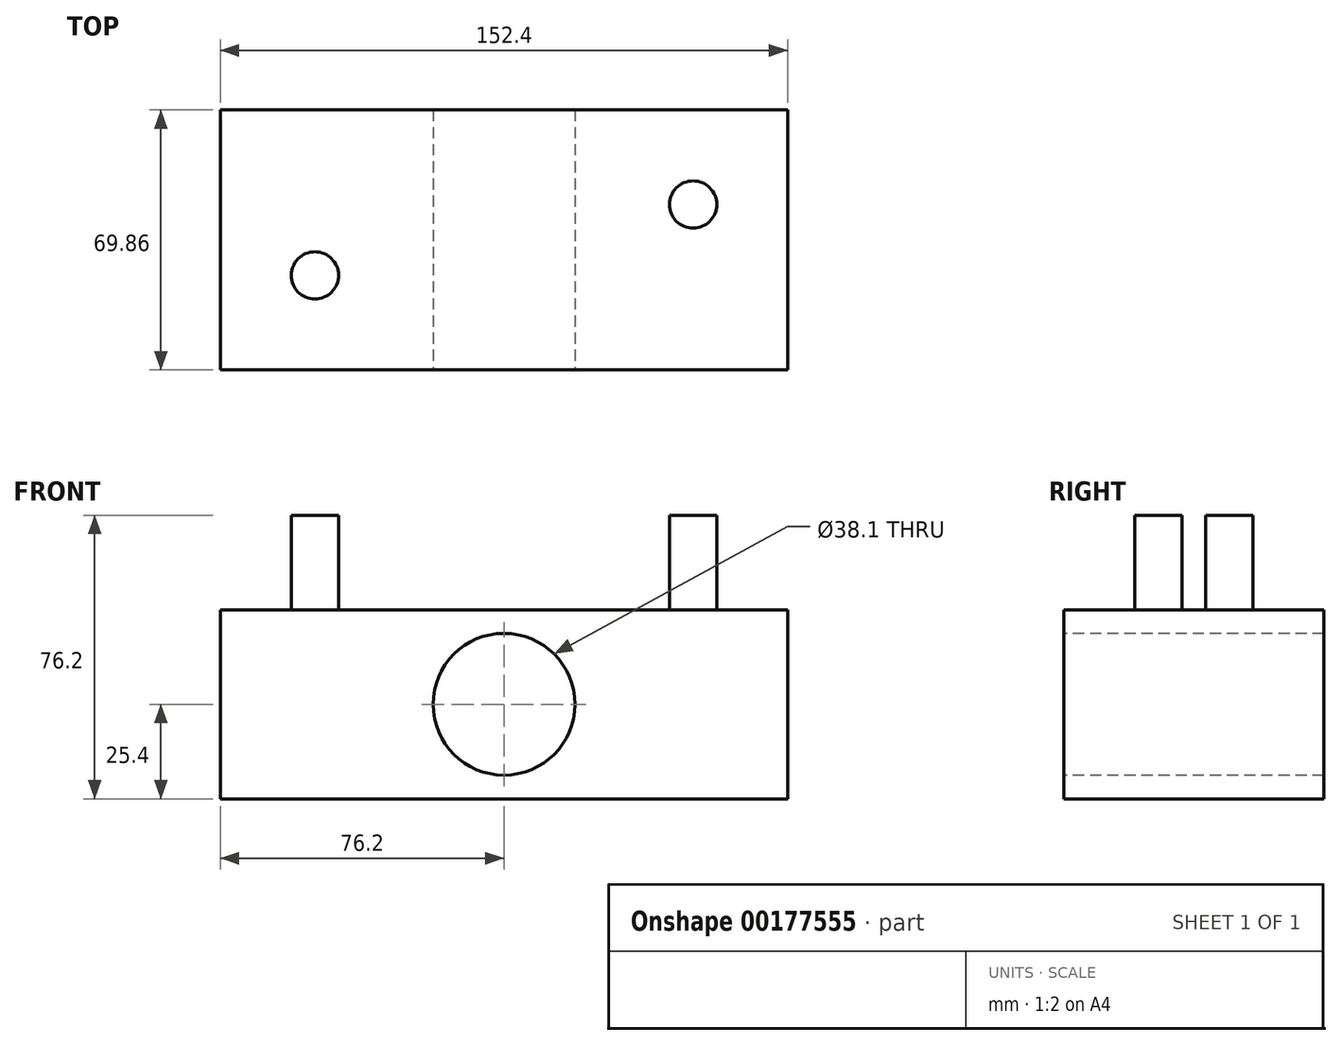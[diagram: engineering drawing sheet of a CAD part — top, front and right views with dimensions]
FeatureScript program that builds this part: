
annotation { "Feature Type Name" : "Feature", "Feature Type Description" : "" }
export const myFeature = defineFeature(function(context is Context, id is Id, definition is map)
    precondition{}
    {
        {
            var Q0;
            Q0=qCreatedBy(makeId("Top.planeOp"),FACE);
            var sketch = newSketch(context, id + "F0", { "sketchPlane" : qUnion([Q0])});
            skLineSegment(sketch, "E0.bottom", {"start": v(76.2, -34.92) * mm, "end": v(-76.2, -34.93) * mm});
            skLineSegment(sketch, "E0.top", {"start": v(76.2, 34.93) * mm, "end": v(-76.2, 34.92) * mm});
            skLineSegment(sketch, "E0.left", {"start": v(76.2, -34.93) * mm, "end": v(76.2, 34.93) * mm});
            skLineSegment(sketch, "E0.right", {"start": v(-76.2, -34.93) * mm, "end": v(-76.2, 34.92) * mm});
            skPoint(sketch, "E0.middle", {"position": v(0, 0) * mm});
            skSolve(sketch);
        }
        {
            var Q0;
            Q0 = qSketchRegion(id + "F0", true);
            extrude(context, id + "F1", {"entities" : qUnion([Q0]), "depth" : 50.8 * mm});
        }
        {
            var Q0;
            Q0=makeQuery(id+"F1.opExtrude","SWEPT_FACE",FACE,{"disambiguationData":[OSD([sQuery(id+"F0.wireOp",EDGE,"E0.bottom")])]});
            var sketch = newSketch(context, id + "F2", { "sketchPlane" : qUnion([Q0])});
            skCircle(sketch, "E1", {"center": v(0, 25.4) * mm, "radius": 19.05 * mm});
            skLineSegment(sketch, "E2", {"start": v(0, 50.8) * mm, "end": v(0, 0) * mm, "construction": true});
            skSolve(sketch);
        }
        {
            var Q0;
            Q0 = qSketchRegion(id + "F2", true);
            extrude(context, id + "F3", {"entities" : qUnion([Q0]), "operationType" : NewBodyOperationType.REMOVE, "oppositeDirection" : true, "depth" : 201.42 * mm});
        }
        {
            var Q0;
            Q0=makeQuery(id+"F1.opExtrude","CAP_FACE",FACE,{"disambiguationData":[OSD([sQuery(id+"F0.wireOp",EDGE,"E0.bottom"),sQuery(id+"F0.wireOp",EDGE,"E0.top"),sQuery(id+"F0.wireOp",EDGE,"E0.left"),sQuery(id+"F0.wireOp",EDGE,"E0.right")])],"isStart":false});
            var sketch = newSketch(context, id + "F4", { "sketchPlane" : qUnion([Q0])});
            skCircle(sketch, "E3", {"center": v(50.8, 9.53) * mm, "radius": 6.35 * mm});
            skCircle(sketch, "E4", {"center": v(-50.8, -9.53) * mm, "radius": 6.35 * mm});
            skSolve(sketch);
        }
        {
            var Q0;
            Q0 = qSketchRegion(id + "F4", true);
            extrude(context, id + "F5", {"entities" : qUnion([Q0]), "operationType" : NewBodyOperationType.ADD, "depth" : 25.4 * mm});
        }
    });
